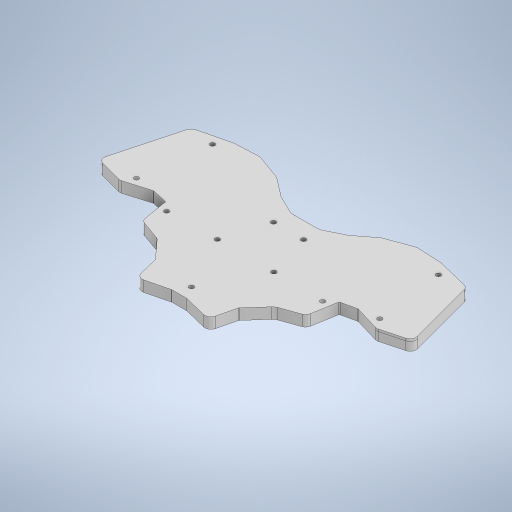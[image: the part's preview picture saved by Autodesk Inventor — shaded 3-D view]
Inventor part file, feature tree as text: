
AUTODESK INVENTOR PART (.ipt)
format: ipt  version: 2024 (Build 280153000, 153)  size: 880,640 bytes
history: native  units: mm
features: reference x93, sketch x5, other x5, extrude x4, plane x2, fillet x2, projected_geometry x2, hole x1, chamfer x1
ambient origin geometry x8: Origin, YZ Plane, XZ Plane, XY Plane, X Axis, Y Axis, Z Axis, Center Point
bodies: Volumenkörper1 (feature_tree)
feature tree (115):
  extrude  "Extrusion1"  Depth=2.0mm TaperAngle=0.0deg
  sketch  "Skizze2"  dims[d4=9.2mm d5=0.0mm]
  plane  "Arbeitsebene1"
  extrude  "Extrusion2"  Depth=9.0mm
  sketch  "Skizze3"  dims[d6=2.2mm d7=6.0mm d8=4.0mm d9=3.0mm d10=90.0deg d11=8.0mm d12=20.594885mm d13=9.0mm]
  plane  "Arbeitsebene2"
  extrude  "Extrusion3"  TaperAngle=0.0deg  [1 undecoded]
  hole  "Bohrung1"  [1 undecoded]
  extrude  "Extrusion4"  Depth=2.0mm
  chamfer  "Fasen1"  Distance=2.5mm
  fillet  "Rundung1"  Radius=2.5mm
  fillet  "Rundung2"  Radius=2.5mm
  sketch  "Skizze1"  dims[d0=2.0mm d1=0.0mm d2=7.2mm d3=0.0mm]
  reference  "Referenz1"
  reference  "Referenz2"
  reference  "Referenz3"
  reference  "Referenz4"
  reference  "Referenz5"
  reference  "Referenz6"
  reference  "Referenz7"
  reference  "Referenz8"
  reference  "Referenz9"
  reference  "Referenz10"
  reference  "Referenz11"
  reference  "Referenz12"
  reference  "Referenz13"
  reference  "Referenz14"
  reference  "Referenz15"
  reference  "Referenz16"
  reference  "Referenz17"
  reference  "Referenz18"
  reference  "Referenz19"
  reference  "Referenz20"
  reference  "Referenz21"
  reference  "Referenz22"
  reference  "Referenz23"
  reference  "Referenz24"
  reference  "Referenz25"
  reference  "Referenz26"
  reference  "Referenz27"
  reference  "Referenz28"
  reference  "Referenz29"
  reference  "Referenz30"
  reference  "Referenz31"
  reference  "Referenz32"
  reference  "Referenz33"
  reference  "Referenz34"
  reference  "Referenz35"
  projected_geometry  "Projizierte Kontur1"
  reference  "Referenz36"
  reference  "Referenz37"
  reference  "Referenz38"
  reference  "Referenz39"
  reference  "Referenz40"
  reference  "Referenz41"
  reference  "Referenz42"
  reference  "Referenz43"
  reference  "Referenz44"
  reference  "Referenz45"
  reference  "Referenz46"
  reference  "Referenz47"
  reference  "Referenz48"
  reference  "Referenz49"
  reference  "Referenz50"
  reference  "Referenz51"
  reference  "Referenz52"
  reference  "Referenz53"
  reference  "Referenz54"
  reference  "Referenz55"
  reference  "Referenz56"
  reference  "Referenz57"
  reference  "Referenz58"
  reference  "Referenz59"
  reference  "Referenz60"
  reference  "Referenz61"
  reference  "Referenz62"
  reference  "Referenz63"
  reference  "Referenz64"
  reference  "Referenz65"
  reference  "Referenz66"
  reference  "Referenz67"
  reference  "Referenz68"
  reference  "Referenz69"
  reference  "Referenz70"
  reference  "Referenz71"
  reference  "Referenz72"
  reference  "Referenz73"
  reference  "Referenz74"
  reference  "Referenz75"
  reference  "Referenz76"
  reference  "Referenz77"
  sketch  "Skizze5"  dims[d14=5.0mm d15=0.0mm d16=0.0mm]
  projected_geometry  "Projizierte Kontur2"
  reference  "Referenz78"
  reference  "Referenz79"
  reference  "Referenz80"
  reference  "Referenz81"
  reference  "Referenz82"
  reference  "Referenz83"
  reference  "Referenz84"
  reference  "Referenz85"
  reference  "Referenz86"
  reference  "Referenz87"
  reference  "Referenz88"
  reference  "Referenz89"
  reference  "Referenz90"
  reference  "Referenz91"
  reference  "Referenz92"
  reference  "Referenz93"
  sketch  "Skizze6"  dims[d17=4.75mm d18=2.0mm d19=45.0deg d20=2.0mm d21=2.0mm d22=2.5mm d23=2.5mm d24=2.5mm d25=2.5mm d26=2.5mm d27=2.5mm d28=2.5mm d29=2.5mm d30=2.5mm d31=2.5mm d32=2.5mm]
  other  "<userpath>\OneDrive\Keyboards\Blavinge\case\1-part\bottom.iam"
  other  "bottom.iam"
  other  "left_bottom:1"
  other  "middle_bottom:1"
  other  "left_bottom_MIR:1"
note: 2 required parameter values undecoded (feature->parameter linkage not recoverable at this tier; creation-order binding heuristic only, values carry confidence <= 0.55)
